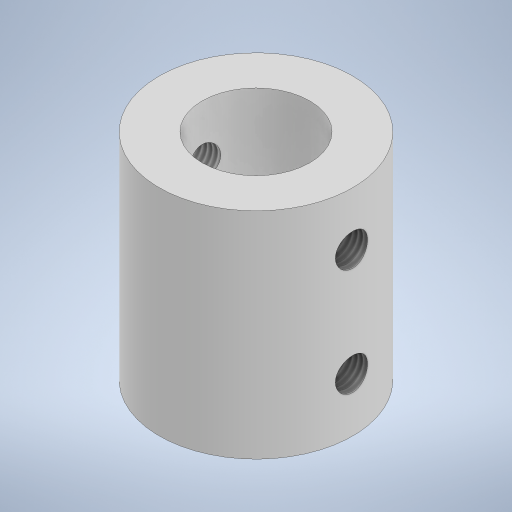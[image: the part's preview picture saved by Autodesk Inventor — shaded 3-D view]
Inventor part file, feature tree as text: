
AUTODESK INVENTOR PART (.ipt)
format: ipt  version: 2023 (Build 270158000, 158)  size: 249,856 bytes
history: native  units: mm
features: extrude x3, sketch x3, thread x2, other x1
ambient origin geometry x8: Origin, YZ Plane, XZ Plane, XY Plane, X Axis, Y Axis, Z Axis, Center Point
bodies: Body1 (feature_tree)
feature tree (9):
  other  "Твердое тело1"
  extrude  "Выдавливание1"  Depth=7.0mm
  extrude  "Выдавливание2"  Depth=18.0mm
  extrude  "Выдавливание3"  Depth=20.0mm TaperAngle=0.0deg
  thread  "Резьба1"
  thread  "Резьба2"
  sketch  "Эскиз1"
  sketch  "Эскиз2"
  sketch  "Эскиз3"
